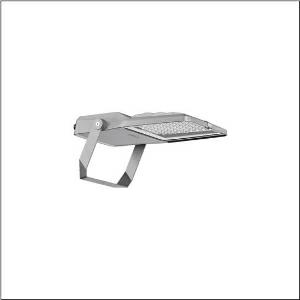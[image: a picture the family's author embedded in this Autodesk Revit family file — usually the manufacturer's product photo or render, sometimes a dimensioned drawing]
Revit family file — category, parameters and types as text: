
# Revit family: floodlight_fl_21_iq_mini___pl52_5xa7772b4d1a_9164
name_source: partatom
category: Lighting Fixtures
units: mm (PartAtom-declared; Revit-internal decimal feet)

## family parameters
Cut with Voids When Loaded = No
Host = Face
Light Source = No
Part Type = Normal
Room Calculation Point = No
Round Connector Dimension = Use Diameter
Shared = No

## types (1)
- --- (1 x LED, 6490 lm, 45.5 W, 4000K)
    Apparent Load = 46 VA
    CIE Flux Codes = 26 60 98 100 100
    Color Rendering = 70
    Color Temperature = 4000K
    Default Elevation = 1800 mm
    Description = Floodlight FL 21 iQ mini, floodlight, primary light control with lens, of PMMA, primary optical cover: protective disc, of toughened safety glass, transparent, light distribution: PL52, light emission: direct distribution, installation type: surface-mounted, LED, High Power LED, rated luminous flux: 6.490lm, luminous efficacy: 143lm/W, light colour: 740, colour temperature: 4000K, control gear: iQ Street-Remote/DALI, control: Street-Remote, Auto-Match, Temp-Guard, Night-Set, Smart-Wire, Desk-Remote (wireless, voltage-free reading and setting of iQ features in the workshop via application-optimized NFC function/RFID function), optimised constant luminous flux control (CLO 2.0), with terminal, 6-pole, mains connection: 220..240V, AC, 50/60Hz, start of lifetime: 46W, end of service life: 48W, reduction: 22W, luminaire housing, of diecast aluminium, powder-coated, Siteco® metallic grey (DB 702S), corrosivity category C5 mid according to DIN EN ISO 12944, suitable for swimming pools, chlorine-resistant, sealing non-destructively replaceable, mounting bracket, of steel, galvanised, powder-coated, Siteco® metallic grey (DB 702S), protection rating (complete): IP66, insulation class (complete): insulation class II (safety insulation), certification: CE, ENEC, VDE, protection symbol: D, impact resistance: IK08, permissible operating ambient temperature: -40..+40°C, permissible operating ambient temperature for outdoor applications: -40..+50°C, standard: DIN EN 12944, LABS conformity tested according to VDMA 24364:2018-05, packaging unit: 1 piece

Light Distribution: PL52
    Height = 70 mm
    Lamp = 1 x LED
    Lamp Light Flux = 6490 lm
    Lamp Power = 45.5 W
    Lamp count = 1
    Length = 485 mm
    Luminous efficacy = 143 lm/W
    Manufacturer = Siteco
    ModVariant = No
    Model = 5XA7772B4D1A
    Number of Poles = 1
    OnlyDefault = Yes
    Power Factor = 1
    Product Name = Floodlight FL 21 iQ mini | PL52
    Product group = floodlight | pylon annexe
    ProductGroupID = 6200
    Protection Class = Protection class II
    Protection Degree = IP 66
    RLX_Detail_Level = 1
    RLX_Emergency_Light_Flux = 0 lm
    RLX_Emergency_Type = 0
    RLX_Emergency_Type_DB = No
    RlxData = <blob elided: 96497 chars, md5=2ba7e080>
    Socket = socket
    Standby Power = 0 W
    System Light Flux = 6490 lm
    System Power = 46 W
    Type Comments = factory setting: luminous flux: 100 % | dim-lin: 254 | 463 mA
    Type Image = l_1006845.jpg
    URL = http://relux.com
    VarID = @adj_164772
    Voltage = 0 V
    Weight = 0.00 kg
    Width = 337 mm

## geometry (parser evidence)
native form markers: Blend x4, Sweep x13
no freeform markers — native parametric forms only
